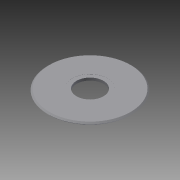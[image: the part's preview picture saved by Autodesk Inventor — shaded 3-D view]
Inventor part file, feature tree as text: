
AUTODESK INVENTOR PART (.ipt)
format: ipt  version: 2014 SP2 (Build 180246200, 246)  size: 6,019,072 bytes
history: native  units: in
note: dims shown in document units (in); Inventor stores cm internally (conversion verified against a paired STEP export)
features: sketch x3, extrude x2, chamfer x1, emboss x1
ambient origin geometry x8: Origin, YZ Plane, XZ Plane, XY Plane, X Axis, Y Axis, Z Axis, Center Point
bodies: Solid1 (feature_tree)
feature tree (7):
  extrude  "Extrusion1"  Depth=0.8in
  extrude  "Extrusion2"  Depth=1.05in
  chamfer  "Chamfer1"  Distance=0.0024in
  emboss  "Emboss2"
  sketch  "Sketch1"  dims[d0=2.5in d1=0.8in]
  sketch  "Sketch2"  dims[d2=0.08in d3=0.0in d4=1.05in d5=0.0024in d6=0.0in]
  sketch  "Sketch4"  dims[d7=0.04in d8=0.125in d9=45.0deg d12=0.04in d13=0.0in]
